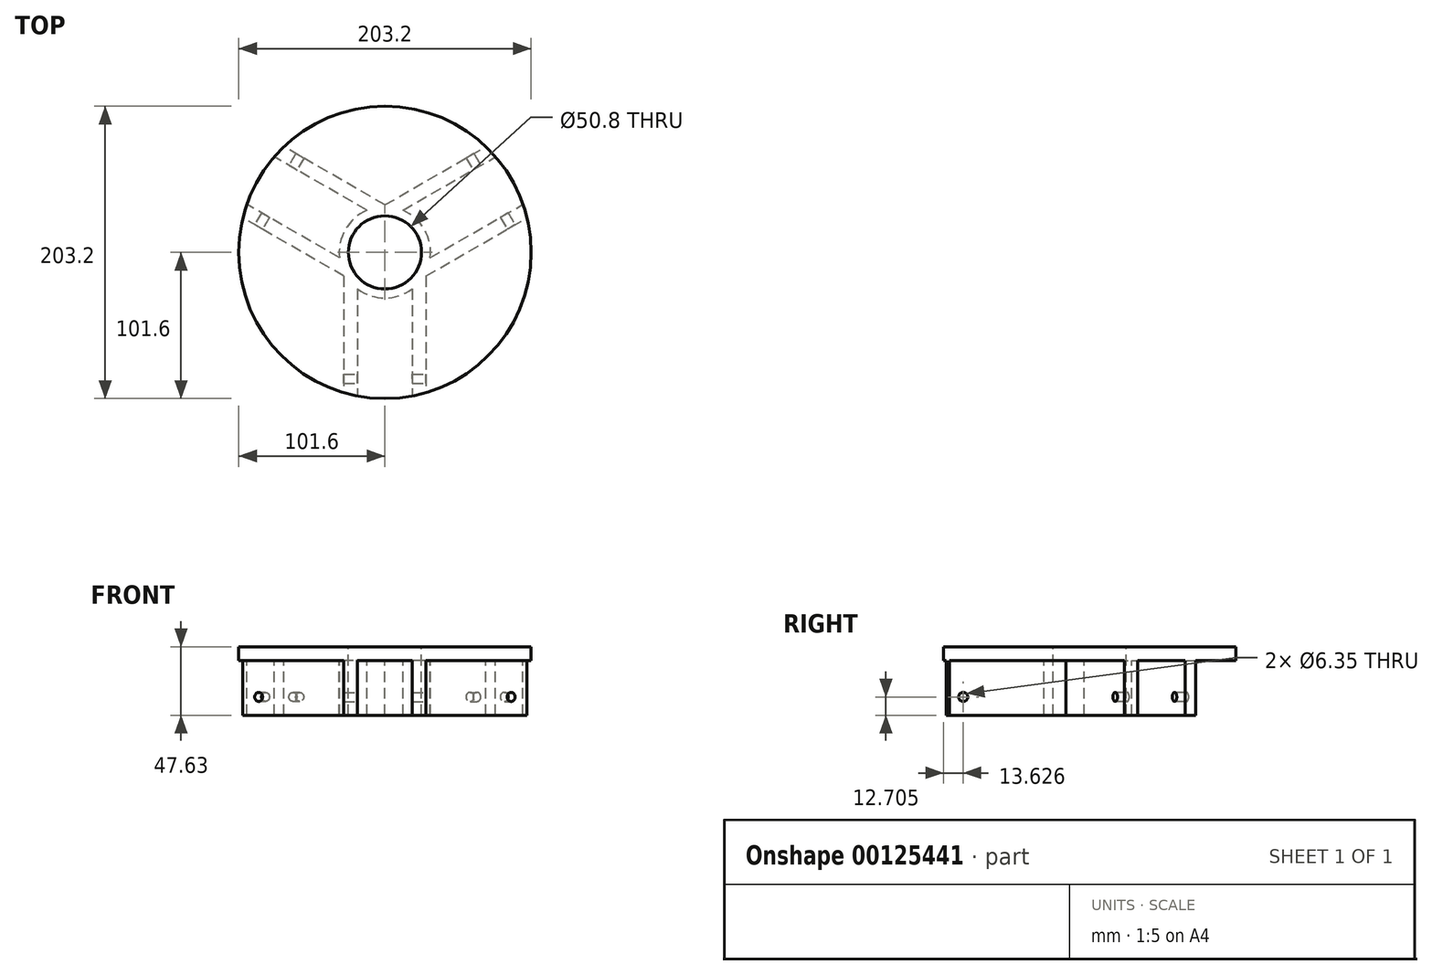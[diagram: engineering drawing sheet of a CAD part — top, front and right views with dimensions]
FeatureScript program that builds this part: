
annotation { "Feature Type Name" : "Feature", "Feature Type Description" : "" }
export const myFeature = defineFeature(function(context is Context, id is Id, definition is map)
    precondition{}
    {
        {
            var Q0;
            Q0=qCreatedBy(makeId("Front.planeOp"),FACE);
            var sketch = newSketch(context, id + "F0", { "sketchPlane" : qUnion([Q0])});
            skLineSegment(sketch, "E0", {"start": v(25.4, 0) * mm, "end": v(101.6, 0) * mm});
            skLineSegment(sketch, "E1", {"start": v(101.6, 0) * mm, "end": v(101.6, -9.53) * mm});
            skLineSegment(sketch, "E2", {"start": v(101.6, -9.53) * mm, "end": v(31.75, -9.53) * mm});
            skLineSegment(sketch, "E3", {"start": v(31.75, -9.53) * mm, "end": v(31.75, -47.63) * mm});
            skLineSegment(sketch, "E4", {"start": v(31.75, -47.63) * mm, "end": v(25.4, -47.63) * mm});
            skLineSegment(sketch, "E5", {"start": v(25.4, -47.63) * mm, "end": v(25.4, 0) * mm});
            skLineSegment(sketch, "E6", {"start": v(0, 0) * mm, "end": v(0, -8.2) * mm});
            skSolve(sketch);
        }
        {
            var Q0;
            Q0=makeQuery(id+"F0.imprint","IMPRINT",FACE,{"disambiguationData":[TD([[makeQuery(id+"F0.imprint","IMPRINT",EDGE,{"derivedFrom":sQuery(id+"F0.wireOp",EDGE,"E0")}),-1.0]])]});
            var Q1;
            Q1=sQuery(id+"F0.wireOp",EDGE,"E6");
            revolve(context, id + "F1", {"entities" : qUnion([Q0]), "axis" : qUnion([Q1]), "revolveType" : RevolveType.FULL});
        }
        {
            var Q0;
            Q0=makeQuery(id+"F1.opRevolve","SWEPT_FACE",FACE,{"disambiguationData":[OSD([sQuery(id+"F0.wireOp",EDGE,"E2")])]});
            var sketch = newSketch(context, id + "F2", { "sketchPlane" : qUnion([Q0])});
            skLineSegment(sketch, "E7", {"start": v(0, 101.6) * mm, "end": v(0, 31.75) * mm});
            skLineSegment(sketch, "E8", {"start": v(0, 0) * mm, "end": v(87.99, -50.8) * mm});
            skLineSegment(sketch, "E9.MirrorCS", {"start": v(0, 0) * mm, "end": v(-87.99, -50.8) * mm});
            skPoint(sketch, "E10.middle", {"position": v(0, 66.68) * mm});
            skLineSegment(sketch, "E11.bottom", {"start": v(19.05, 25.4) * mm, "end": v(-19.05, 25.4) * mm});
            skLineSegment(sketch, "E11.top", {"start": v(19.05, 107.95) * mm, "end": v(-19.05, 107.95) * mm});
            skLineSegment(sketch, "E11.left", {"start": v(19.05, 25.4) * mm, "end": v(19.05, 107.95) * mm});
            skLineSegment(sketch, "E11.right", {"start": v(-19.05, 25.4) * mm, "end": v(-19.05, 107.95) * mm});
            skLineSegment(sketch, "E12", {"start": v(-12.47, -29.2) * mm, "end": v(-76.9, -66.4) * mm});
            skLineSegment(sketch, "E13", {"start": v(-31.52, 3.8) * mm, "end": v(-95.95, -33.4) * mm});
            skLineSegment(sketch, "E14", {"start": v(2.3, -31.67) * mm, "end": v(-70.15, -73.5) * mm});
            skLineSegment(sketch, "E15", {"start": v(-26.27, 17.83) * mm, "end": v(-98.72, -24) * mm});
            skLineSegment(sketch, "E16", {"start": v(-28.58, 13.84) * mm, "end": v(-28.58, 97.5) * mm});
            skLineSegment(sketch, "E17.MirrorCS", {"start": v(31.52, 3.8) * mm, "end": v(95.95, -33.4) * mm});
            skLineSegment(sketch, "E18.MirrorCS", {"start": v(-2.3, -31.67) * mm, "end": v(70.15, -73.5) * mm});
            skLineSegment(sketch, "E19.MirrorCS", {"start": v(26.27, 17.83) * mm, "end": v(98.72, -24) * mm});
            skLineSegment(sketch, "E20.MirrorCS", {"start": v(12.47, -29.2) * mm, "end": v(76.9, -66.4) * mm});
            skLineSegment(sketch, "E21.MirrorCS", {"start": v(28.58, 13.84) * mm, "end": v(28.57, 97.5) * mm});
            skLineSegment(sketch, "E22", {"start": v(-27.5, -15.87) * mm, "end": v(-87.99, -50.8) * mm});
            skLineSegment(sketch, "E23", {"start": v(27.5, -15.87) * mm, "end": v(87.99, -50.8) * mm});
            skCircle(sketch, "E24", {"center": v(0, 66.68) * mm, "radius": 3.18 * mm});
            skCircle(sketch, "E25", {"center": v(-57.74, -33.34) * mm, "radius": 3.18 * mm});
            skCircle(sketch, "E26", {"center": v(57.74, -33.34) * mm, "radius": 3.18 * mm});
            skSolve(sketch);
        }
        {
            var Q0;
            {var subQ0=sQuery(id+"F2.wireOp",EDGE,"E13");Q0=makeQuery(id+"F2.imprint","IMPRINT",FACE,{"disambiguationData":[TD([[makeQuery(id+"F2.imprint","IMPRINT",EDGE,{"derivedFrom":subQ0}),-1.0]])]});}
            var Q1;
            {var subQ0=sQuery(id+"F2.wireOp",EDGE,"E12");Q1=makeQuery(id+"F2.imprint","IMPRINT",FACE,{"disambiguationData":[TD([[makeQuery(id+"F2.imprint","IMPRINT",EDGE,{"derivedFrom":subQ0}),1.0]])]});}
            var Q2;
            {var subQ0=sQuery(id+"F2.wireOp",EDGE,"E18.MirrorCS");Q2=makeQuery(id+"F2.imprint","IMPRINT",FACE,{"disambiguationData":[TD([[makeQuery(id+"F2.imprint","IMPRINT",EDGE,{"derivedFrom":subQ0}),1.0]])]});}
            var Q3;
            {var subQ0=sQuery(id+"F2.wireOp",EDGE,"E17.MirrorCS");Q3=makeQuery(id+"F2.imprint","IMPRINT",FACE,{"disambiguationData":[TD([[makeQuery(id+"F2.imprint","IMPRINT",EDGE,{"derivedFrom":subQ0}),1.0]])]});}
            var Q4;
            {var subQ6=sQuery(id+"F2.wireOp",EDGE,"E16");Q4=makeQuery(id+"F2.imprint","IMPRINT",FACE,{"disambiguationData":[TD([[makeQuery(id+"F2.imprint","IMPRINT",EDGE,{"derivedFrom":subQ6}),-1.0]])]});}
            var Q5;
            {var subQ6=sQuery(id+"F2.wireOp",EDGE,"E21.MirrorCS");Q5=makeQuery(id+"F2.imprint","IMPRINT",FACE,{"disambiguationData":[TD([[makeQuery(id+"F2.imprint","IMPRINT",EDGE,{"derivedFrom":subQ6}),1.0]])]});}
            var Q6;
            {var subQ0=sQuery(id+"F2.wireOp",EDGE,"E16");var subQ8=sQuery(id+"F2.wireOp",EDGE,"E15");var subQ10=makeQuery(id+"F2.imprint","INTERSECT",VERTEX,{"derivedFrom":[subQ8,subQ0]});Q6=makeQuery(id+"F2.imprint","IMPRINT",FACE,{"disambiguationData":[TD([[makeQuery(id+"F2.imprint","IMPRINT",EDGE,{"disambiguationData":[TD([[subQ10,1.0]])],"derivedFrom":subQ8}),-1.0]])]});}
            var Q7;
            {var subQ0=sQuery(id+"F2.wireOp",EDGE,"E21.MirrorCS");var subQ8=sQuery(id+"F2.wireOp",EDGE,"E19.MirrorCS");var subQ9=makeQuery(id+"F2.imprint","INTERSECT",VERTEX,{"derivedFrom":[subQ8,subQ0]});Q7=makeQuery(id+"F2.imprint","IMPRINT",FACE,{"disambiguationData":[TD([[makeQuery(id+"F2.imprint","IMPRINT",EDGE,{"disambiguationData":[TD([[subQ9,1.0]])],"derivedFrom":subQ8}),1.0]])]});}
            var Q8;
            {var subQ4=sQuery(id+"F2.wireOp",EDGE,"E20.MirrorCS");Q8=makeQuery(id+"F2.imprint","IMPRINT",FACE,{"disambiguationData":[TD([[makeQuery(id+"F2.imprint","IMPRINT",EDGE,{"derivedFrom":subQ4}),-1.0]])]});}
            extrude(context, id + "F3", {"entities" : qUnion([Q0, Q1, Q2, Q3, Q4, Q5, Q6, Q7, Q8]), "operationType" : NewBodyOperationType.ADD, "depth" : 38.1 * mm});
        }
        {
            var Q0;
            Q0=makeQuery(id+"F3.opExtrude","SWEPT_FACE",FACE,{"disambiguationData":[OSD([sQuery(id+"F2.wireOp",EDGE,"E21.MirrorCS")])]});
            var sketch = newSketch(context, id + "F4", { "sketchPlane" : qUnion([Q0])});
            skCircle(sketch, "E27", {"center": v(-87.97, -34.93) * mm, "radius": 3.18 * mm});
            skSolve(sketch);
        }
        {
            var Q0;
            Q0 = qSketchRegion(id + "F4", true);
            extrude(context, id + "F5", {"entities" : qUnion([Q0]), "operationType" : NewBodyOperationType.REMOVE, "oppositeDirection" : true, "depth" : 76.2 * mm});
        }
        {
            var Q0;
            Q0=makeQuery(id+"F3.opExtrude","SWEPT_FACE",FACE,{"disambiguationData":[OSD([sQuery(id+"F2.wireOp",EDGE,"E19.MirrorCS")])]});
            var sketch = newSketch(context, id + "F6", { "sketchPlane" : qUnion([Q0])});
            skCircle(sketch, "E28", {"center": v(84.8, -34.93) * mm, "radius": 3.18 * mm});
            skSolve(sketch);
        }
        {
            var Q0;
            Q0 = qSketchRegion(id + "F6", true);
            extrude(context, id + "F7", {"entities" : qUnion([Q0]), "operationType" : NewBodyOperationType.REMOVE, "oppositeDirection" : true, "depth" : 76.2 * mm});
        }
        {
            var Q0;
            Q0=makeQuery(id+"F3.opExtrude","SWEPT_FACE",FACE,{"disambiguationData":[OSD([sQuery(id+"F2.wireOp",EDGE,"E15")])]});
            var sketch = newSketch(context, id + "F8", { "sketchPlane" : qUnion([Q0])});
            skCircle(sketch, "E29", {"center": v(-84.8, -34.93) * mm, "radius": 3.18 * mm});
            skSolve(sketch);
        }
        {
            var Q0;
            Q0 = qSketchRegion(id + "F8", true);
            extrude(context, id + "F9", {"entities" : qUnion([Q0]), "operationType" : NewBodyOperationType.REMOVE, "oppositeDirection" : true, "depth" : 76.2 * mm});
        }
    });
